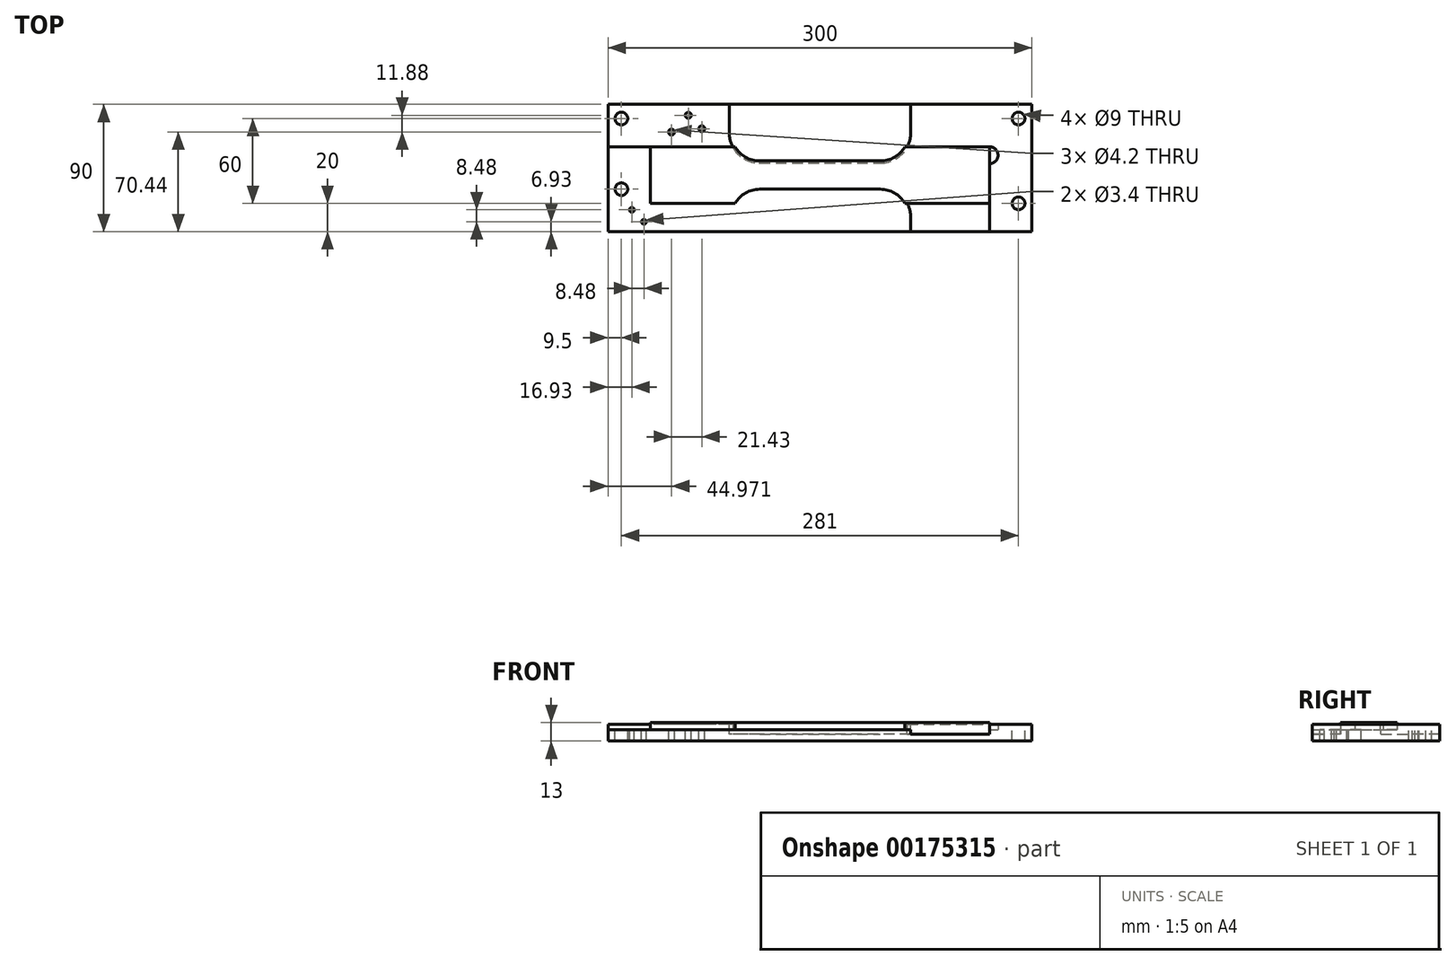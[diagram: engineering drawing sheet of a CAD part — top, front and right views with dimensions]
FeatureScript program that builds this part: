
annotation { "Feature Type Name" : "Feature", "Feature Type Description" : "" }
export const myFeature = defineFeature(function(context is Context, id is Id, definition is map)
    precondition{}
    {
        {
            var Q0;
            Q0=qCreatedBy(makeId("Top.planeOp"),FACE);
            var sketch = newSketch(context, id + "F0", { "sketchPlane" : qUnion([Q0])});
            skLineSegment(sketch, "E0.bottom", {"start": v(0, 0) * mm, "end": v(120, 0) * mm});
            skLineSegment(sketch, "E0.top", {"start": v(60, -20) * mm, "end": v(120, -20) * mm});
            skLineSegment(sketch, "E0.left", {"start": v(0, 0) * mm, "end": v(0, -10) * mm});
            skLineSegment(sketch, "E0.right", {"start": v(120, 0) * mm, "end": v(120, -20) * mm});
            skLineSegment(sketch, "E1", {"start": v(0, -10) * mm, "end": v(42.68, -10) * mm});
            skArc(sketch, "E2", {"start": v(60, -20) * mm, "mid": v(52.68, -12.68) * mm, "end": v(42.68, -10) * mm});
            skLineSegment(sketch, "E3.MirrorCS", {"start": v(120, 0) * mm, "end": v(120, 20) * mm});
            skLineSegment(sketch, "E4.MirrorCS", {"start": v(60, 20) * mm, "end": v(120, 20) * mm});
            skArc(sketch, "E5.MirrorCS", {"start": v(60, 20) * mm, "mid": v(52.68, 12.68) * mm, "end": v(42.68, 10) * mm});
            skLineSegment(sketch, "E6.MirrorCS", {"start": v(0, 10) * mm, "end": v(42.68, 10) * mm});
            skLineSegment(sketch, "E7.MirrorCS", {"start": v(0, -10) * mm, "end": v(-42.68, -10) * mm});
            skArc(sketch, "E8.MirrorCS", {"start": v(-60, -20) * mm, "mid": v(-52.68, -12.68) * mm, "end": v(-42.68, -10) * mm});
            skLineSegment(sketch, "E9.MirrorCS", {"start": v(-60, -20) * mm, "end": v(-120, -20) * mm});
            skLineSegment(sketch, "E10.MirrorCS", {"start": v(-120, 0) * mm, "end": v(-120, -20) * mm});
            skLineSegment(sketch, "E11.MirrorCS", {"start": v(-120, 0) * mm, "end": v(-120, 20) * mm});
            skLineSegment(sketch, "E12.MirrorCS", {"start": v(-60, 20) * mm, "end": v(-120, 20) * mm});
            skArc(sketch, "E13.MirrorCS", {"start": v(-60, 20) * mm, "mid": v(-52.68, 12.68) * mm, "end": v(-42.68, 10) * mm});
            skLineSegment(sketch, "E14.MirrorCS", {"start": v(0, 10) * mm, "end": v(-42.68, 10) * mm});
            skSolve(sketch);
        }
        {
            var Q0;
            Q0=makeQuery(id+"F0.imprint","IMPRINT",FACE,{"disambiguationData":[TD([[makeQuery(id+"F0.imprint","IMPRINT",EDGE,{"derivedFrom":sQuery(id+"F0.wireOp",EDGE,"E0.bottom")}),1.0]])]});
            var Q1;
            Q1=makeQuery(id+"F0.imprint","IMPRINT",FACE,{"disambiguationData":[TD([[makeQuery(id+"F0.imprint","IMPRINT",EDGE,{"derivedFrom":sQuery(id+"F0.wireOp",EDGE,"E0.bottom")}),-1.0]])]});
            extrude(context, id + "F1", {"entities" : qUnion([Q0, Q1]), "depth" : 5 * mm});
        }
        {
            var Q0;
            Q0=makeQuery(id+"F1.opExtrude","CAP_FACE",FACE,{"disambiguationData":[OSD([sQuery(id+"F0.wireOp",EDGE,"E0.top"),sQuery(id+"F0.wireOp",EDGE,"E0.right"),sQuery(id+"F0.wireOp",EDGE,"E1"),sQuery(id+"F0.wireOp",EDGE,"E2"),sQuery(id+"F0.wireOp",EDGE,"E3.MirrorCS"),sQuery(id+"F0.wireOp",EDGE,"E4.MirrorCS"),sQuery(id+"F0.wireOp",EDGE,"E5.MirrorCS"),sQuery(id+"F0.wireOp",EDGE,"E6.MirrorCS"),sQuery(id+"F0.wireOp",EDGE,"E7.MirrorCS"),sQuery(id+"F0.wireOp",EDGE,"E8.MirrorCS"),sQuery(id+"F0.wireOp",EDGE,"E9.MirrorCS"),sQuery(id+"F0.wireOp",EDGE,"E10.MirrorCS"),sQuery(id+"F0.wireOp",EDGE,"E11.MirrorCS"),sQuery(id+"F0.wireOp",EDGE,"E12.MirrorCS"),sQuery(id+"F0.wireOp",EDGE,"E13.MirrorCS"),sQuery(id+"F0.wireOp",EDGE,"E14.MirrorCS")])],"isStart":true});
            var sketch = newSketch(context, id + "F2", { "sketchPlane" : qUnion([Q0])});
            skArc(sketch, "E15.0", {"start": v(64.18, 30) * mm, "mid": v(57.88, 14.8) * mm, "end": v(42.68, 8.5) * mm});
            skLineSegment(sketch, "E15.1", {"start": v(42.68, 8.5) * mm, "end": v(-42.68, 8.5) * mm});
            skArc(sketch, "E15.2", {"start": v(-64.18, 30) * mm, "mid": v(-57.88, 14.8) * mm, "end": v(-42.68, 8.5) * mm});
            skArc(sketch, "E16.0", {"start": v(64.18, -30) * mm, "mid": v(57.88, -14.8) * mm, "end": v(42.68, -8.5) * mm});
            skLineSegment(sketch, "E16.1", {"start": v(-42.68, -8.5) * mm, "end": v(42.68, -8.5) * mm});
            skArc(sketch, "E16.2", {"start": v(-64.18, -30) * mm, "mid": v(-57.88, -14.8) * mm, "end": v(-42.68, -8.5) * mm});
            skLineSegment(sketch, "E17.bottom", {"start": v(150, 30) * mm, "end": v(-150, 30) * mm});
            skLineSegment(sketch, "E17.top", {"start": v(150, -30) * mm, "end": v(-150, -30) * mm});
            skLineSegment(sketch, "E17.left", {"start": v(150, 30) * mm, "end": v(150, -30) * mm});
            skLineSegment(sketch, "E17.right", {"start": v(-150, 30) * mm, "end": v(-150, -30) * mm});
            skPoint(sketch, "E17.middle", {"position": v(0, 0) * mm});
            skLineSegment(sketch, "E18.bottom", {"start": v(120, -20) * mm, "end": v(61.71, -20) * mm});
            skLineSegment(sketch, "E18.top", {"start": v(120, 20) * mm, "end": v(61.71, 20) * mm});
            skLineSegment(sketch, "E18.left", {"start": v(120, -20) * mm, "end": v(120, 20) * mm});
            skLineSegment(sketch, "E18.right", {"start": v(-120, -20) * mm, "end": v(-120, 20) * mm});
            skLineSegment(sketch, "E19.trimOffspring", {"start": v(-61.71, -20) * mm, "end": v(-120, -20) * mm});
            skLineSegment(sketch, "E20.trimOffspring", {"start": v(-61.71, 20) * mm, "end": v(-120, 20) * mm});
            skLineSegment(sketch, "E21", {"start": v(120, 20) * mm, "end": v(120, 30) * mm});
            skArc(sketch, "E22", {"start": v(120, -20) * mm, "mid": v(126, -14) * mm, "end": v(120, -8) * mm});
            skLineSegment(sketch, "E23", {"start": v(-120, -20) * mm, "end": v(-150, -20) * mm});
            skSolve(sketch);
        }
        {
            var Q0;
            Q0=makeQuery(id+"F2.imprint","IMPRINT",FACE,{"disambiguationData":[TD([[makeQuery(id+"F2.imprint","IMPRINT",EDGE,{"derivedFrom":sQuery(id+"F2.wireOp",EDGE,"E15.0")}),1.0]])]});
            var Q1;
            {var subQ12=sQuery(id+"F2.wireOp",EDGE,"E15.1");Q1=makeQuery(id+"F2.imprint","IMPRINT",FACE,{"disambiguationData":[TD([[makeQuery(id+"F2.imprint","IMPRINT",EDGE,{"derivedFrom":subQ12}),1.0]])]});}
            var Q2;
            {var subQ3=sQuery(id+"F2.wireOp",EDGE,"E17.right");Q2=makeQuery(id+"F2.imprint","IMPRINT",FACE,{"disambiguationData":[TD([[makeQuery(id+"F2.imprint","IMPRINT",EDGE,{"derivedFrom":subQ3}),1.0]])]});}
            var Q3;
            {var subQ0=sQuery(id+"F2.wireOp",EDGE,"E17.left");Q3=makeQuery(id+"F2.imprint","IMPRINT",FACE,{"disambiguationData":[TD([[makeQuery(id+"F2.imprint","IMPRINT",EDGE,{"derivedFrom":subQ0}),-1.0]])]});}
            var Q4;
            {var subQ0=sQuery(id+"F2.wireOp",EDGE,"E22");Q4=makeQuery(id+"F2.imprint","IMPRINT",FACE,{"disambiguationData":[TD([[makeQuery(id+"F2.imprint","IMPRINT",EDGE,{"derivedFrom":subQ0}),1.0]])]});}
            var Q5;
            Q5=makeQuery(id+"F2.imprint","IMPRINT",FACE,{"disambiguationData":[TD([[makeQuery(id+"F2.imprint","IMPRINT",EDGE,{"derivedFrom":sQuery(id+"F2.wireOp",EDGE,"E18.right")}),-1.0]])]});
            extrude(context, id + "F3", {"entities" : qUnion([Q0, Q1, Q2, Q3, Q4, Q5]), "depth" : 3 * mm});
        }
        {
            var Q0;
            Q0=makeQuery(id+"F3.opExtrude","CAP_FACE",FACE,{"disambiguationData":[OSD([sQuery(id+"F2.wireOp",EDGE,"E15.0"),sQuery(id+"F2.wireOp",EDGE,"E15.1"),sQuery(id+"F2.wireOp",EDGE,"E15.2"),sQuery(id+"F2.wireOp",EDGE,"E16.0"),sQuery(id+"F2.wireOp",EDGE,"E16.1"),sQuery(id+"F2.wireOp",EDGE,"E16.2"),sQuery(id+"F2.wireOp",EDGE,"IRfECljg-vqVa-0TSg-P9bU-STEebCYjBjKk.bottom"),sQuery(id+"F2.wireOp",EDGE,"IRfECljg-vqVa-0TSg-P9bU-STEebCYjBjKk.top"),sQuery(id+"F2.wireOp",EDGE,"IRfECljg-vqVa-0TSg-P9bU-STEebCYjBjKk.left"),sQuery(id+"F2.wireOp",EDGE,"IRfECljg-vqVa-0TSg-P9bU-STEebCYjBjKk.right"),sQuery(id+"F2.wireOp",EDGE,"4bbe4a13-bd5d-4cc3-8af1-a1c493cf100e.trimOffspring"),sQuery(id+"F2.wireOp",EDGE,"6966df2d-3bc1-4cae-9169-fa0aedf4a5a6.trimOffspring")])],"isStart":false});
            var sketch = newSketch(context, id + "F4", { "sketchPlane" : qUnion([Q0])});
            skLineSegment(sketch, "E24.bottom", {"start": v(130, -30) * mm, "end": v(-130, -30) * mm});
            skLineSegment(sketch, "E24.top", {"start": v(130, 30) * mm, "end": v(-130, 30) * mm});
            skLineSegment(sketch, "E24.left", {"start": v(130, -30) * mm, "end": v(130, 30) * mm});
            skLineSegment(sketch, "E24.right", {"start": v(-130, -30) * mm, "end": v(-130, 30) * mm});
            skPoint(sketch, "E24.middle", {"position": v(0, 0) * mm});
            skSolve(sketch);
        }
        {
            var Q0;
            Q0=makeQuery(id+"F4.imprint","IMPRINT",FACE,{"disambiguationData":[TD([[makeQuery(id+"F4.imprint","IMPRINT",EDGE,{"derivedFrom":sQuery(id+"F4.wireOp",EDGE,"E24.bottom")}),-1.0]])]});
            var Q1;
            Q1=makeQuery(id+"F4.imprint","IMPRINT",FACE,{"disambiguationData":[TD([[makeQuery(id+"F4.imprint","IMPRINT",EDGE,{"derivedFrom":makeQuery(id+"F3.opExtrude","CAP_EDGE",EDGE,{"disambiguationData":[OSD([sQuery(id+"F2.wireOp",EDGE,"59ab3319-c9ba-4cde-8ec8-90ca6e909526.0")])],"isStart":false})}),-1.0]])]});
            var Q2;
            Q2=makeQuery(id+"F4.imprint","IMPRINT",FACE,{"disambiguationData":[TD([[makeQuery(id+"F4.imprint","IMPRINT",EDGE,{"derivedFrom":makeQuery(id+"F3.opExtrude","CAP_EDGE",EDGE,{"disambiguationData":[OSD([sQuery(id+"F2.wireOp",EDGE,"E15.0")])],"isStart":false})}),1.0]])]});
            var Q3;
            {var subQ1=makeQuery(id+"F3.opExtrude","CAP_EDGE",EDGE,{"disambiguationData":[OSD([sQuery(id+"F2.wireOp",EDGE,"E15.0")])],"isStart":false});Q3=makeQuery(id+"F4.imprint","IMPRINT",FACE,{"disambiguationData":[TD([[makeQuery(id+"F4.imprint","IMPRINT",EDGE,{"derivedFrom":subQ1}),-1.0]])]});}
            var Q4;
            {var subQ1=makeQuery(id+"F3.opExtrude","CAP_EDGE",EDGE,{"disambiguationData":[OSD([sQuery(id+"F2.wireOp",EDGE,"E16.0")])],"isStart":false});Q4=makeQuery(id+"F4.imprint","IMPRINT",FACE,{"disambiguationData":[TD([[makeQuery(id+"F4.imprint","IMPRINT",EDGE,{"derivedFrom":subQ1}),1.0]])]});}
            var Q5;
            {var subQ0=sQuery(id+"F4.wireOp",EDGE,"E24.right");Q5=makeQuery(id+"F4.imprint","IMPRINT",FACE,{"disambiguationData":[TD([[makeQuery(id+"F4.imprint","IMPRINT",EDGE,{"derivedFrom":subQ0}),1.0]])]});}
            var Q6;
            {var subQ0=sQuery(id+"F4.wireOp",EDGE,"E24.left");Q6=makeQuery(id+"F4.imprint","IMPRINT",FACE,{"disambiguationData":[TD([[makeQuery(id+"F4.imprint","IMPRINT",EDGE,{"derivedFrom":subQ0}),-1.0]])]});}
            extrude(context, id + "F5", {"entities" : qUnion([Q0, Q1, Q2, Q3, Q4, Q5, Q6]), "operationType" : NewBodyOperationType.ADD, "depth" : 5 * mm});
        }
        {
            var Q0;
            {var subQ0=sQuery(id+"F2.wireOp",EDGE,"E17.left");Q0=makeQuery(id+"F2.imprint","IMPRINT",FACE,{"disambiguationData":[TD([[makeQuery(id+"F2.imprint","IMPRINT",EDGE,{"derivedFrom":subQ0}),-1.0]])]});}
            var Q1;
            {var subQ0=sQuery(id+"F2.wireOp",EDGE,"E19.trimOffspring");Q1=makeQuery(id+"F2.imprint","IMPRINT",FACE,{"disambiguationData":[TD([[makeQuery(id+"F2.imprint","IMPRINT",EDGE,{"derivedFrom":subQ0}),1.0]])]});}
            extrude(context, id + "F6", {"entities" : qUnion([Q0, Q1]), "operationType" : NewBodyOperationType.ADD, "oppositeDirection" : true, "depth" : 4 * mm});
        }
        {
            var Q0;
            {var subQ0=sQuery(id+"F2.wireOp",EDGE,"E17.top");var subQ1=makeQuery(id+"F2.imprint","IMPRINT",EDGE,{"disambiguationData":[TD([[makeQuery(id+"F2.imprint","INTERSECT",VERTEX,{"derivedFrom":[sQuery(id+"F2.wireOp",EDGE,"E16.2"),subQ0]}),-1.0]])],"derivedFrom":subQ0});var subQ2=makeQuery(id+"F2.imprint","IMPRINT",EDGE,{"disambiguationData":[TD([[makeQuery(id+"F2.imprint","INTERSECT",VERTEX,{"derivedFrom":[sQuery(id+"F2.wireOp",EDGE,"E16.0"),subQ0]}),1.0]])],"derivedFrom":subQ0});Q0=makeQuery(id+"F6.boolean.opBoolean","MERGE",FACE,{"derivedFrom":[makeQuery(id+"F5.boolean.opBoolean","MERGE",FACE,{"derivedFrom":[makeQuery(id+"F3.opExtrude","SWEPT_FACE",FACE,{"disambiguationData":[OSD([subQ0]),TDD([subQ2])]}),makeQuery(id+"F3.opExtrude","SWEPT_FACE",FACE,{"disambiguationData":[OSD([subQ0]),TDD([subQ1])]}),makeQuery(id+"F5.opExtrude","SWEPT_FACE",FACE,{"disambiguationData":[OSD([subQ0,sQuery(id+"F4.wireOp",EDGE,"E24.bottom")])]})]}),makeQuery(id+"F6.opExtrude","SWEPT_FACE",FACE,{"disambiguationData":[OSD([subQ0]),TDD([subQ2])]}),makeQuery(id+"F6.opExtrude","SWEPT_FACE",FACE,{"disambiguationData":[OSD([subQ0]),TDD([subQ1])]})]});}
            extrude(context, id + "F7", {"entities" : qUnion([Q0]), "operationType" : NewBodyOperationType.ADD, "depth" : 20 * mm});
        }
        {
            var Q0;
            {var subQ0=sQuery(id+"F2.wireOp",EDGE,"E17.top");var subQ1=sQuery(id+"F2.wireOp",EDGE,"E16.2");var subQ2=sQuery(id+"F2.wireOp",EDGE,"E17.right");Q0=makeQuery(id+"F7.boolean.opBoolean","MERGE",FACE,{"derivedFrom":[makeQuery(id+"F6.opExtrude","CAP_FACE",FACE,{"disambiguationData":[OSD([subQ1,subQ0,subQ2,sQuery(id+"F2.wireOp",EDGE,"E19.trimOffspring"),sQuery(id+"F2.wireOp",EDGE,"E23")])],"isStart":false}),makeQuery(id+"F7.opExtrude","SWEPT_FACE",FACE,{"disambiguationData":[OSD([subQ0]),TDD([makeQuery(id+"F6.opExtrude","CAP_EDGE",EDGE,{"disambiguationData":[OSD([subQ0]),TDD([makeQuery(id+"F2.imprint","IMPRINT",EDGE,{"disambiguationData":[TD([[makeQuery(id+"F2.imprint","INTERSECT",VERTEX,{"derivedFrom":[subQ1,subQ0]}),-1.0]])],"derivedFrom":subQ0})])],"isStart":false})])]})]});}
            var sketch = newSketch(context, id + "F8", { "sketchPlane" : qUnion([Q0])});
            skCircle(sketch, "E25", {"center": v(-83.6, 32.78) * mm, "radius": 2.1 * mm});
            skCircle(sketch, "E26", {"center": v(-105.03, 30.44) * mm, "radius": 2.1 * mm});
            skCircle(sketch, "E27", {"center": v(-93.15, 42.32) * mm, "radius": 2.1 * mm});
            skLineSegment(sketch, "E28", {"start": v(0, 65.01) * mm, "end": v(0, 0) * mm});
            skCircle(sketch, "E29.MirrorC", {"center": v(83.6, 32.78) * mm, "radius": 2.1 * mm});
            skCircle(sketch, "E30.MirrorC", {"center": v(93.15, 42.32) * mm, "radius": 2.1 * mm});
            skCircle(sketch, "E31.MirrorC", {"center": v(105.03, 30.44) * mm, "radius": 2.1 * mm});
            skSolve(sketch);
        }
        {
            var Q0;
            Q0=makeQuery(id+"F8.imprint","IMPRINT",FACE,{"disambiguationData":[TD([[makeQuery(id+"F8.imprint","IMPRINT",EDGE,{"derivedFrom":sQuery(id+"F8.wireOp",EDGE,"E26")}),1.0]])]});
            var Q1;
            Q1=makeQuery(id+"F8.imprint","IMPRINT",FACE,{"disambiguationData":[TD([[makeQuery(id+"F8.imprint","IMPRINT",EDGE,{"derivedFrom":sQuery(id+"F8.wireOp",EDGE,"E27")}),1.0]])]});
            var Q2;
            Q2=makeQuery(id+"F8.imprint","IMPRINT",FACE,{"disambiguationData":[TD([[makeQuery(id+"F8.imprint","IMPRINT",EDGE,{"derivedFrom":sQuery(id+"F8.wireOp",EDGE,"E25")}),1.0]])]});
            var Q3;
            Q3=makeQuery(id+"F8.imprint","IMPRINT",FACE,{"disambiguationData":[TD([[makeQuery(id+"F8.imprint","IMPRINT",EDGE,{"derivedFrom":sQuery(id+"F8.wireOp",EDGE,"E29.MirrorC")}),-1.0]])]});
            var Q4;
            Q4=makeQuery(id+"F8.imprint","IMPRINT",FACE,{"disambiguationData":[TD([[makeQuery(id+"F8.imprint","IMPRINT",EDGE,{"derivedFrom":sQuery(id+"F8.wireOp",EDGE,"E30.MirrorC")}),-1.0]])]});
            var Q5;
            Q5=makeQuery(id+"F8.imprint","IMPRINT",FACE,{"disambiguationData":[TD([[makeQuery(id+"F8.imprint","IMPRINT",EDGE,{"derivedFrom":sQuery(id+"F8.wireOp",EDGE,"E31.MirrorC")}),-1.0]])]});
            var Q6;
            Q6=sQuery(id+"F8.wireOp",EDGE,"E26");
            var Q7;
            Q7=sQuery(id+"F8.wireOp",EDGE,"E27");
            var Q8;
            Q8=sQuery(id+"F8.wireOp",EDGE,"E25");
            extrude(context, id + "F9", {"entities" : qUnion([Q0, Q1, Q2, Q3, Q4, Q5]), "operationType" : NewBodyOperationType.REMOVE, "surfaceEntities" : qUnion([Q6, Q7, Q8]), "oppositeDirection" : true, "depth" : 25 * mm});
        }
        {
            var Q0;
            Q0=makeQuery(id+"F1.opExtrude","CAP_FACE",FACE,{"disambiguationData":[OSD([sQuery(id+"F0.wireOp",EDGE,"E0.top"),sQuery(id+"F0.wireOp",EDGE,"E0.right"),sQuery(id+"F0.wireOp",EDGE,"E1"),sQuery(id+"F0.wireOp",EDGE,"E2"),sQuery(id+"F0.wireOp",EDGE,"E3.MirrorCS"),sQuery(id+"F0.wireOp",EDGE,"E4.MirrorCS"),sQuery(id+"F0.wireOp",EDGE,"E5.MirrorCS"),sQuery(id+"F0.wireOp",EDGE,"E6.MirrorCS"),sQuery(id+"F0.wireOp",EDGE,"E7.MirrorCS"),sQuery(id+"F0.wireOp",EDGE,"E8.MirrorCS"),sQuery(id+"F0.wireOp",EDGE,"E9.MirrorCS"),sQuery(id+"F0.wireOp",EDGE,"E10.MirrorCS"),sQuery(id+"F0.wireOp",EDGE,"E11.MirrorCS"),sQuery(id+"F0.wireOp",EDGE,"E12.MirrorCS"),sQuery(id+"F0.wireOp",EDGE,"E13.MirrorCS"),sQuery(id+"F0.wireOp",EDGE,"E14.MirrorCS")])],"isStart":false});
            var sketch = newSketch(context, id + "F10", { "sketchPlane" : qUnion([Q0])});
            skCircle(sketch, "E32", {"center": v(-140.5, -10) * mm, "radius": 4.5 * mm});
            skCircle(sketch, "E33", {"center": v(140.5, -20) * mm, "radius": 4.5 * mm});
            skCircle(sketch, "E34.0.1.0", {"center": v(140.5, 40) * mm, "radius": 4.5 * mm});
            skCircle(sketch, "E34.0.1.1", {"center": v(-140.5, 40) * mm, "radius": 4.5 * mm});
            skSolve(sketch);
        }
        {
            var Q0;
            Q0=makeQuery(id+"F10.imprint","IMPRINT",FACE,{"disambiguationData":[TD([[makeQuery(id+"F10.imprint","IMPRINT",EDGE,{"derivedFrom":sQuery(id+"F10.wireOp",EDGE,"E32")}),1.0]])]});
            var Q1;
            Q1=makeQuery(id+"F10.imprint","IMPRINT",FACE,{"disambiguationData":[TD([[makeQuery(id+"F10.imprint","IMPRINT",EDGE,{"derivedFrom":sQuery(id+"F10.wireOp",EDGE,"E33")}),1.0]])]});
            var Q2;
            Q2=makeQuery(id+"F10.imprint","IMPRINT",FACE,{"disambiguationData":[TD([[makeQuery(id+"F10.imprint","IMPRINT",EDGE,{"derivedFrom":sQuery(id+"F10.wireOp",EDGE,"E34.0.1.1")}),1.0]])]});
            var Q3;
            Q3=makeQuery(id+"F10.imprint","IMPRINT",FACE,{"disambiguationData":[TD([[makeQuery(id+"F10.imprint","IMPRINT",EDGE,{"derivedFrom":sQuery(id+"F10.wireOp",EDGE,"E34.0.1.0")}),1.0]])]});
            var Q4;
            Q4=sQuery(id+"F10.wireOp",EDGE,"E32");
            var Q5;
            Q5=sQuery(id+"F10.wireOp",EDGE,"E33");
            extrude(context, id + "F11", {"entities" : qUnion([Q0, Q1, Q2, Q3]), "operationType" : NewBodyOperationType.REMOVE, "surfaceEntities" : qUnion([Q4, Q5]), "oppositeDirection" : true, "depth" : 25 * mm});
        }
        {
            var Q0;
            Q0=makeQuery(id+"F3.opExtrude","CAP_FACE",FACE,{"disambiguationData":[OSD([sQuery(id+"F2.wireOp",EDGE,"E15.0"),sQuery(id+"F2.wireOp",EDGE,"E15.1"),sQuery(id+"F2.wireOp",EDGE,"E15.2"),sQuery(id+"F2.wireOp",EDGE,"E16.0"),sQuery(id+"F2.wireOp",EDGE,"E16.1"),sQuery(id+"F2.wireOp",EDGE,"E16.2"),sQuery(id+"F2.wireOp",EDGE,"E17.bottom"),sQuery(id+"F2.wireOp",EDGE,"E17.top"),sQuery(id+"F2.wireOp",EDGE,"E17.left"),sQuery(id+"F2.wireOp",EDGE,"E17.right")])],"isStart":true});
            var sketch = newSketch(context, id + "F12", { "sketchPlane" : qUnion([Q0])});
            skLineSegment(sketch, "E35.bottom", {"start": v(120, 20) * mm, "end": v(-120, 20) * mm});
            skLineSegment(sketch, "E35.top", {"start": v(120, -20) * mm, "end": v(-120, -20) * mm});
            skLineSegment(sketch, "E35.left", {"start": v(120, 20) * mm, "end": v(120, -20) * mm});
            skLineSegment(sketch, "E35.right", {"start": v(-120, 20) * mm, "end": v(-120, -20) * mm});
            skCircle(sketch, "E36", {"center": v(-124.59, -33.07) * mm, "radius": 1.7 * mm});
            skCircle(sketch, "E37", {"center": v(-133.07, -24.59) * mm, "radius": 1.7 * mm});
            skSolve(sketch);
        }
        {
            var Q0;
            {var subQ0=sQuery(id+"F2.wireOp",EDGE,"E17.bottom");Q0=makeQuery(id+"F6.boolean.opBoolean","MERGE",FACE,{"derivedFrom":[makeQuery(id+"F5.boolean.opBoolean","MERGE",FACE,{"derivedFrom":[makeQuery(id+"F3.opExtrude","SWEPT_FACE",FACE,{"disambiguationData":[OSD([subQ0]),TDD([makeQuery(id+"F2.imprint","IMPRINT",EDGE,{"disambiguationData":[TD([[makeQuery(id+"F2.imprint","INTERSECT",VERTEX,{"derivedFrom":[subQ0,sQuery(id+"F2.wireOp",EDGE,"E17.left")]}),-1.0]])],"derivedFrom":subQ0}),makeQuery(id+"F2.imprint","IMPRINT",EDGE,{"disambiguationData":[TD([[makeQuery(id+"F2.imprint","INTERSECT",VERTEX,{"derivedFrom":[sQuery(id+"F2.wireOp",EDGE,"E15.0"),subQ0]}),1.0]])],"derivedFrom":subQ0})])]}),makeQuery(id+"F3.opExtrude","SWEPT_FACE",FACE,{"disambiguationData":[OSD([subQ0]),TDD([makeQuery(id+"F2.imprint","IMPRINT",EDGE,{"disambiguationData":[TD([[makeQuery(id+"F2.imprint","INTERSECT",VERTEX,{"derivedFrom":[sQuery(id+"F2.wireOp",EDGE,"E15.2"),subQ0]}),-1.0]])],"derivedFrom":subQ0})])]}),makeQuery(id+"F5.opExtrude","SWEPT_FACE",FACE,{"disambiguationData":[OSD([subQ0,sQuery(id+"F4.wireOp",EDGE,"E24.top")])]})]}),makeQuery(id+"F6.opExtrude","SWEPT_FACE",FACE,{"disambiguationData":[OSD([subQ0])]})]});}
            extrude(context, id + "F13", {"entities" : qUnion([Q0]), "operationType" : NewBodyOperationType.ADD, "depth" : 10 * mm});
        }
        {
            var Q0;
            Q0=makeQuery(id+"F12.imprint","IMPRINT",FACE,{"disambiguationData":[TD([[makeQuery(id+"F12.imprint","IMPRINT",EDGE,{"derivedFrom":sQuery(id+"F12.wireOp",EDGE,"E36")}),1.0]])]});
            var Q1;
            Q1=makeQuery(id+"F12.imprint","IMPRINT",FACE,{"disambiguationData":[TD([[makeQuery(id+"F12.imprint","IMPRINT",EDGE,{"derivedFrom":sQuery(id+"F12.wireOp",EDGE,"E37")}),1.0]])]});
            extrude(context, id + "F14", {"entities" : qUnion([Q0, Q1]), "operationType" : NewBodyOperationType.REMOVE, "oppositeDirection" : true, "depth" : 25 * mm});
        }
    });
